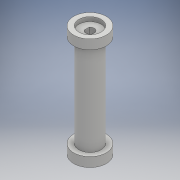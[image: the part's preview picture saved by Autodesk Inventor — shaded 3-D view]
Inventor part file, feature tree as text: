
AUTODESK INVENTOR PART (.ipt)
format: ipt  version: 2017 (Build 210142000, 142)  size: 198,656 bytes
history: native  units: mm
features: sketch x7, extrude x6, revolve x1
ambient origin geometry x8: Origin, YZ Plane, XZ Plane, XY Plane, X Axis, Y Axis, Z Axis, Center Point
bodies: Body1 (feature_tree)
feature tree (14):
  revolve  "Revolution2"  [1 undecoded]
  extrude  "Extrusion6"  Depth=20.0mm
  extrude  "Extrusion7"  Depth=4.0mm
  extrude  "Extrusion11"  Depth=2.5mm
  extrude  "Extrusion12"  Depth=4.0mm
  extrude  "Extrusion13"  Depth=20.0mm
  extrude  "Extrusion14"  Depth=15.0mm
  sketch  "Sketch1"  dims[d1=2.5mm d2=4.0mm]
  sketch  "Sketch6"  dims[d3=7.0mm d4=20.0mm]
  sketch  "Sketch7"  dims[d5=34.0mm d9=4.0mm]
  sketch  "Sketch11"  dims[d12=2.5mm d13=4.0mm]
  sketch  "Sketch12"  dims[d55=22.5mm d56=4.0mm]
  sketch  "Sketch13"  dims[d57=90.0deg d64=20.0mm]
  sketch  "Sketch14"  dims[d65=90.0deg d69=15.0mm d71=15.0mm d73=5.0mm d74=0.0mm d75=2.5mm d76=5.0mm d77=5.0mm d78=26.0mm d79=0.0mm d80=3.0mm d81=3.0mm d82=3.0mm d83=3.0mm d90=19.0mm d91=100.0mm d92=0.0mm d93=2.5mm d94=0.0mm d95=30.0mm d96=0.0mm d97=19.0mm d98=13.0mm d99=2.5mm d100=0.0mm]
note: 1 required parameter value undecoded (feature->parameter linkage not recoverable at this tier; creation-order binding heuristic only, values carry confidence <= 0.55)
